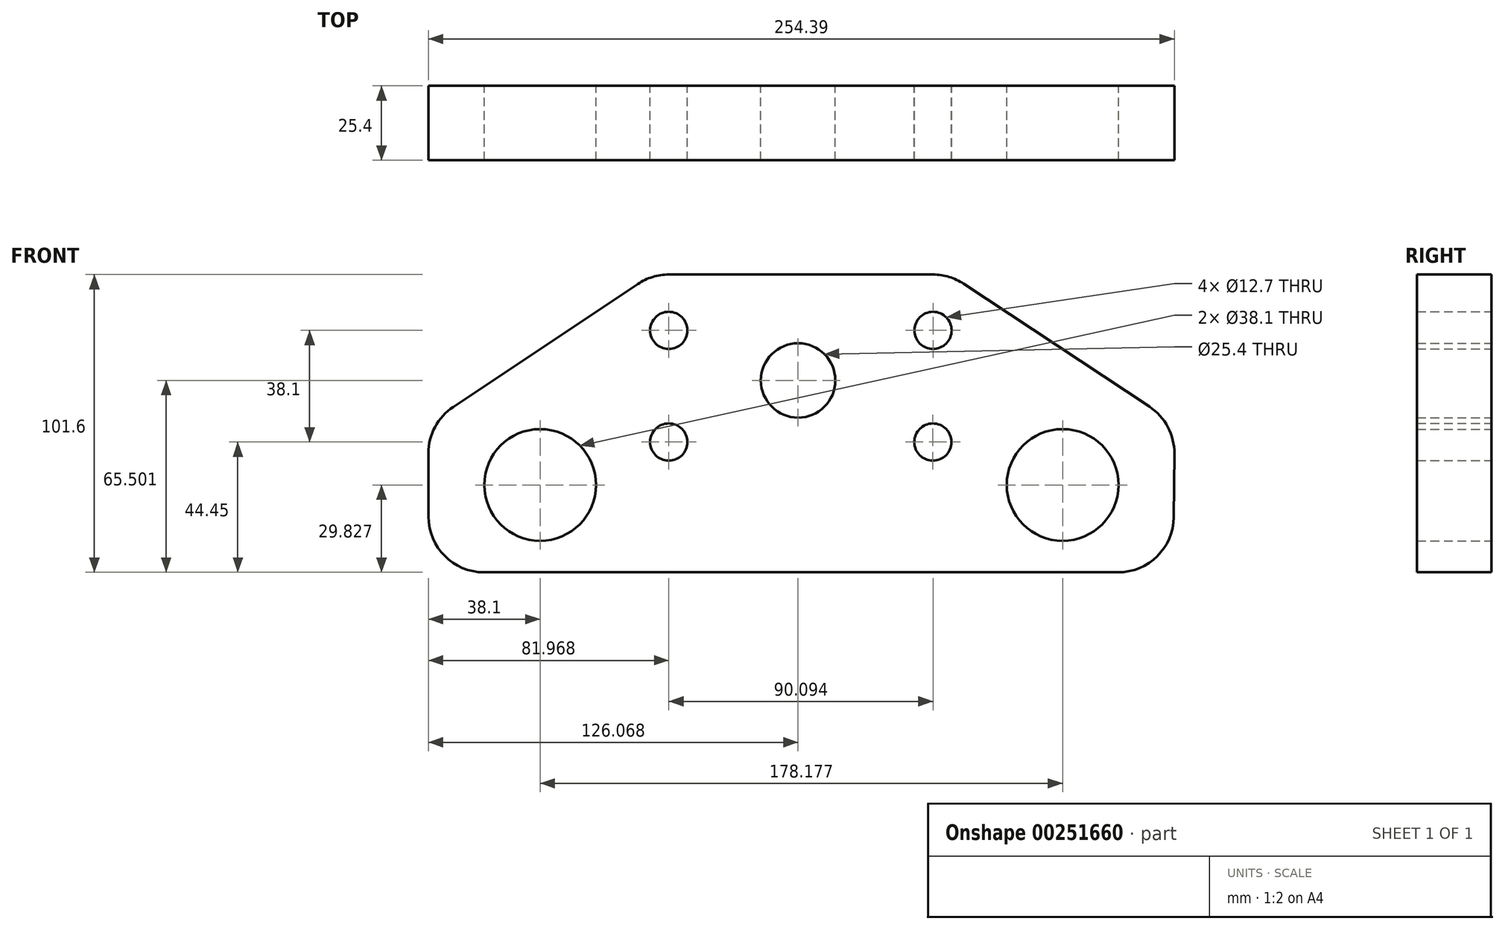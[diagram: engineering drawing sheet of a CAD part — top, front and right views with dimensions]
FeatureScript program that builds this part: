
annotation { "Feature Type Name" : "Feature", "Feature Type Description" : "" }
export const myFeature = defineFeature(function(context is Context, id is Id, definition is map)
    precondition{}
    {
        {
            var Q0;
            Q0=qCreatedBy(makeId("Front.planeOp"),FACE);
            var sketch = newSketch(context, id + "F3", { "sketchPlane" : qUnion([Q0])});
            skLineSegment(sketch, "E0", {"start": v(19.05, 0) * mm, "end": v(235.13, 0) * mm});
            skLineSegment(sketch, "E1", {"start": v(254.18, 18.87) * mm, "end": v(254.39, 40.45) * mm});
            skLineSegment(sketch, "E2", {"start": v(0, 19.05) * mm, "end": v(0, 40.6) * mm});
            skPoint(sketch, "E3", {"position": v(0, 0) * mm});
            skLineSegment(sketch, "E4", {"start": v(127, 101.6) * mm, "end": v(127, 0) * mm, "construction": true});
            skPoint(sketch, "E4.startSnap0", {"position": v(127, 0) * mm});
            skLineSegment(sketch, "E5", {"start": v(127, 101.6) * mm, "end": v(172.06, 101.6) * mm});
            skLineSegment(sketch, "E6", {"start": v(127, 101.6) * mm, "end": v(81.97, 101.6) * mm});
            skLineSegment(sketch, "E7", {"start": v(71.4, 98.4) * mm, "end": v(8.48, 56.46) * mm});
            skLineSegment(sketch, "E8", {"start": v(182.58, 98.43) * mm, "end": v(245.86, 56.51) * mm});
            skPoint(sketch, "E9.visualSharp", {"position": v(254.48, 50.8) * mm});
            skArc(sketch, "E9.filletArc", {"start": v(254.39, 40.45) * mm, "mid": v(252.16, 49.56) * mm, "end": v(245.86, 56.51) * mm});
            skPoint(sketch, "E10.visualSharp", {"position": v(254, 0) * mm});
            skArc(sketch, "E10.filletArc", {"start": v(235.13, 0) * mm, "mid": v(248.54, 5.52) * mm, "end": v(254.18, 18.87) * mm});
            skPoint(sketch, "E11.visualSharp", {"position": v(177.8, 101.6) * mm});
            skArc(sketch, "E11.filletArc", {"start": v(182.58, 98.43) * mm, "mid": v(177.56, 100.8) * mm, "end": v(172.06, 101.6) * mm});
            skPoint(sketch, "E12.visualSharp", {"position": v(76.2, 101.6) * mm});
            skArc(sketch, "E12.filletArc", {"start": v(81.97, 101.6) * mm, "mid": v(76.45, 100.78) * mm, "end": v(71.4, 98.4) * mm});
            skPoint(sketch, "E13.visualSharp", {"position": v(0, 50.8) * mm});
            skArc(sketch, "E13.filletArc", {"start": v(8.48, 56.46) * mm, "mid": v(2.25, 49.6) * mm, "end": v(0, 40.6) * mm});
            skArc(sketch, "E14.filletArc", {"start": v(0, 19.05) * mm, "mid": v(5.58, 5.58) * mm, "end": v(19.05, 0) * mm});
            skLineSegment(sketch, "E15", {"start": v(0, 29.83) * mm, "end": v(38.1, 29.83) * mm, "construction": true});
            skCircle(sketch, "E16", {"center": v(38.1, 29.83) * mm, "radius": 19.05 * mm});
            skLineSegment(sketch, "E17", {"start": v(254.39, 29.66) * mm, "end": v(216.29, 29.66) * mm, "construction": true});
            skPoint(sketch, "E17.startSnap0", {"position": v(254.28, 29.66) * mm});
            skCircle(sketch, "E18", {"center": v(216.28, 29.83) * mm, "radius": 19.05 * mm});
            skLineSegment(sketch, "E19", {"start": v(127, 101.6) * mm, "end": v(127, 63.5) * mm});
            skCircle(sketch, "E20", {"center": v(126.07, 65.5) * mm, "radius": 12.7 * mm});
            skLineSegment(sketch, "E21", {"start": v(81.97, 44.45) * mm, "end": v(81.97, 82.55) * mm});
            skLineSegment(sketch, "E22.MirrorCS", {"start": v(172.03, 44.45) * mm, "end": v(172.03, 82.55) * mm});
            skCircle(sketch, "E23", {"center": v(81.97, 82.55) * mm, "radius": 6.35 * mm});
            skCircle(sketch, "E24", {"center": v(81.97, 44.45) * mm, "radius": 6.35 * mm});
            skCircle(sketch, "E25", {"center": v(172.06, 82.55) * mm, "radius": 6.35 * mm});
            skCircle(sketch, "E26", {"center": v(172.03, 44.45) * mm, "radius": 6.35 * mm});
            skSolve(sketch);
        }
        {
            var Q0;
            Q0=makeQuery(id+"F3.imprint","IMPRINT",FACE,{"disambiguationData":[TD([[makeQuery(id+"F3.imprint","IMPRINT",EDGE,{"derivedFrom":sQuery(id+"F3.wireOp",EDGE,"E0")}),1.0]])]});
            extrude(context, id + "F4", {"entities" : qUnion([Q0]), "depth" : 25.4 * mm});
        }
    });
